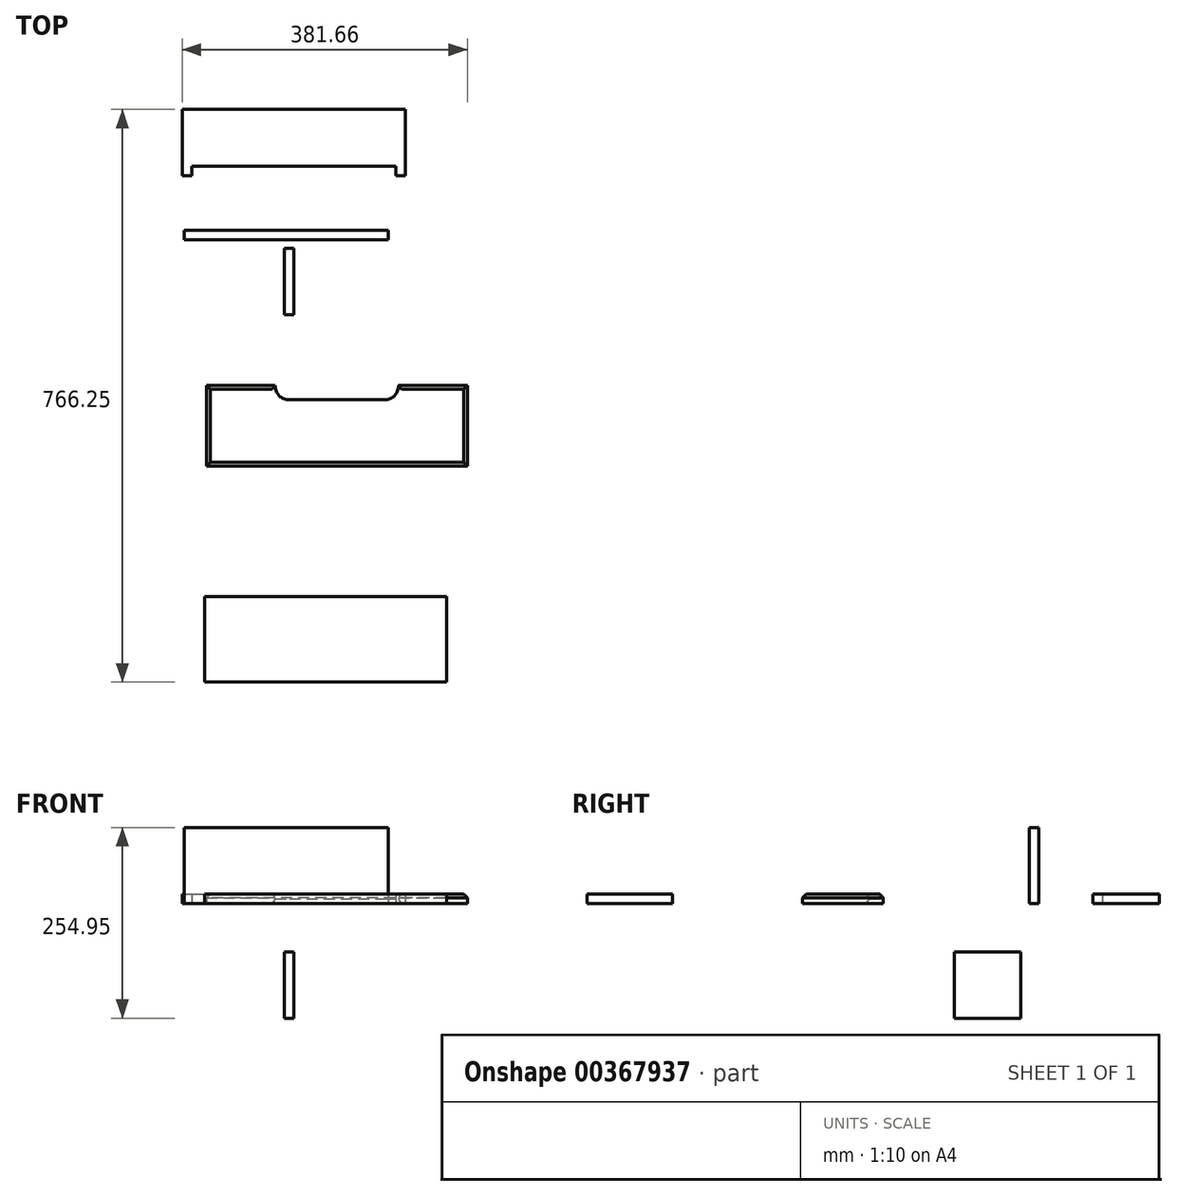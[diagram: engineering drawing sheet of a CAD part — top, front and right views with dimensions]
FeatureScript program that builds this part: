
annotation { "Feature Type Name" : "Feature", "Feature Type Description" : "" }
export const myFeature = defineFeature(function(context is Context, id is Id, definition is map)
    precondition{}
    {
        {
            var Q0;
            Q0=qCreatedBy(makeId("Front.planeOp"),FACE);
            var sketch = newSketch(context, id + "F0", { "sketchPlane" : qUnion([Q0])});
            skLineSegment(sketch, "E0.bottom", {"start": v(-133.55, 101.26) * mm, "end": v(139.5, 101.26) * mm});
            skLineSegment(sketch, "E0.top", {"start": v(-133.55, -0.34) * mm, "end": v(139.5, -0.34) * mm});
            skLineSegment(sketch, "E0.left", {"start": v(-133.55, 101.26) * mm, "end": v(-133.55, -0.34) * mm});
            skLineSegment(sketch, "E0.right", {"start": v(139.5, 101.26) * mm, "end": v(139.5, -0.34) * mm});
            skSolve(sketch);
        }
        {
            var Q0;
            Q0=makeQuery(id+"F0.imprint","IMPRINT",FACE,{"disambiguationData":[TD([[makeQuery(id+"F0.imprint","IMPRINT",EDGE,{"derivedFrom":sQuery(id+"F0.wireOp",EDGE,"E0.bottom")}),-1.0]])]});
            extrude(context, id + "F1", {"entities" : qUnion([Q0]), "depth" : 12.7 * mm});
        }
        {
            var Q0;
            Q0=qCreatedBy(makeId("Top.planeOp"),FACE);
            var sketch = newSketch(context, id + "F2", { "sketchPlane" : qUnion([Q0])});
            skLineSegment(sketch, "E1.bottom", {"start": v(-136.52, 161.62) * mm, "end": v(161.93, 161.62) * mm});
            skLineSegment(sketch, "E1.top", {"start": v(-123.82, 85.42) * mm, "end": v(149.23, 85.42) * mm});
            skLineSegment(sketch, "E1.left", {"start": v(-136.52, 161.62) * mm, "end": v(-136.52, 85.42) * mm});
            skLineSegment(sketch, "E1.right", {"start": v(161.93, 161.62) * mm, "end": v(161.93, 85.42) * mm});
            skLineSegment(sketch, "E2.top", {"start": v(161.93, 72.72) * mm, "end": v(149.23, 72.72) * mm});
            skLineSegment(sketch, "E2.left", {"start": v(161.93, 85.42) * mm, "end": v(161.93, 72.72) * mm});
            skLineSegment(sketch, "E2.right", {"start": v(149.23, 85.42) * mm, "end": v(149.23, 72.72) * mm});
            skLineSegment(sketch, "E3.top", {"start": v(-136.52, 72.72) * mm, "end": v(-123.82, 72.72) * mm});
            skLineSegment(sketch, "E3.left", {"start": v(-136.52, 85.42) * mm, "end": v(-136.52, 72.72) * mm});
            skLineSegment(sketch, "E3.right", {"start": v(-123.82, 85.42) * mm, "end": v(-123.82, 72.72) * mm});
            skSolve(sketch);
        }
        {
            var Q0;
            Q0=makeQuery(id+"F2.imprint","IMPRINT",FACE,{"disambiguationData":[TD([[makeQuery(id+"F2.imprint","IMPRINT",EDGE,{"derivedFrom":sQuery(id+"F2.wireOp",EDGE,"E1.bottom")}),-1.0]])]});
            extrude(context, id + "F3", {"entities" : qUnion([Q0]), "depth" : 12.7 * mm});
        }
        {
            var Q0;
            Q0=qCreatedBy(makeId("Right.planeOp"),FACE);
            var sketch = newSketch(context, id + "F4", { "sketchPlane" : qUnion([Q0])});
            skLineSegment(sketch, "E4.bottom", {"start": v(-24.25, -64.79) * mm, "end": v(-113.15, -64.79) * mm});
            skLineSegment(sketch, "E4.top", {"start": v(-24.25, -153.69) * mm, "end": v(-113.15, -153.69) * mm});
            skLineSegment(sketch, "E4.left", {"start": v(-24.25, -64.79) * mm, "end": v(-24.25, -153.69) * mm});
            skLineSegment(sketch, "E4.right", {"start": v(-113.15, -64.79) * mm, "end": v(-113.15, -153.69) * mm});
            skSolve(sketch);
        }
        {
            var Q0;
            Q0=makeQuery(id+"F4.imprint","IMPRINT",FACE,{"disambiguationData":[TD([[makeQuery(id+"F4.imprint","IMPRINT",EDGE,{"derivedFrom":sQuery(id+"F4.wireOp",EDGE,"E4.bottom")}),1.0]])]});
            extrude(context, id + "F5", {"entities" : qUnion([Q0]), "depth" : 12.7 * mm});
        }
        {
            var Q0;
            Q0=qCreatedBy(makeId("Top.planeOp"),FACE);
            var sketch = newSketch(context, id + "F6", { "sketchPlane" : qUnion([Q0])});
            skLineSegment(sketch, "E5.bottom", {"start": v(-104.11, -207.94) * mm, "end": v(-12.04, -207.94) * mm});
            skLineSegment(sketch, "E5.top", {"start": v(-104.11, -315.89) * mm, "end": v(245.14, -315.89) * mm});
            skLineSegment(sketch, "E5.left", {"start": v(-104.11, -207.94) * mm, "end": v(-104.11, -315.89) * mm});
            skLineSegment(sketch, "E5.right", {"start": v(245.14, -207.94) * mm, "end": v(245.14, -315.89) * mm});
            skArc(sketch, "E6.0.startCap", {"start": v(7.01, -226.99) * mm, "mid": v(-6.46, -221.4) * mm, "end": v(-12.04, -207.94) * mm});
            skArc(sketch, "E6.0.endCap", {"start": v(153.06, -207.94) * mm, "mid": v(147.48, -221.4) * mm, "end": v(134.01, -226.99) * mm});
            skLineSegment(sketch, "E6.0.right", {"start": v(7.01, -226.99) * mm, "end": v(134.01, -226.99) * mm});
            skLineSegment(sketch, "E7.trimOffspring", {"start": v(153.06, -207.94) * mm, "end": v(245.14, -207.94) * mm});
            skSolve(sketch);
        }
        {
            var Q0;
            Q0 = qSketchRegion(id + "F6", true);
            extrude(context, id + "F7", {"entities" : qUnion([Q0]), "depth" : 12.7 * mm});
        }
        {
            var Q0;
            Q0=makeQuery(id+"F7.opExtrude","CAP_EDGE",EDGE,{"disambiguationData":[OSD([sQuery(id+"F6.wireOp",EDGE,"E6.0.right")])],"isStart":false});
            var Q1;
            Q1=makeQuery(id+"F7.opExtrude","CAP_EDGE",EDGE,{"disambiguationData":[OSD([sQuery(id+"F6.wireOp",EDGE,"E6.0.right")])],"isStart":true});
            fillet(context, id + "F8", {"entities" : qUnion([Q0, Q1]), "radius" : 7.62 * mm, "tangentPropagation" : true, "allowEdgeOverflow" : false});
        }
        {
            var Q0;
            Q0=makeQuery(id+"F7.opExtrude","CAP_EDGE",EDGE,{"disambiguationData":[OSD([sQuery(id+"F6.wireOp",EDGE,"E5.bottom")])],"isStart":false});
            var Q1;
            Q1=makeQuery(id+"F7.opExtrude","CAP_EDGE",EDGE,{"disambiguationData":[OSD([sQuery(id+"F6.wireOp",EDGE,"E5.left")])],"isStart":false});
            var Q2;
            Q2=makeQuery(id+"F7.opExtrude","CAP_EDGE",EDGE,{"disambiguationData":[OSD([sQuery(id+"F6.wireOp",EDGE,"E5.top")])],"isStart":false});
            var Q3;
            Q3=makeQuery(id+"F7.opExtrude","CAP_EDGE",EDGE,{"disambiguationData":[OSD([sQuery(id+"F6.wireOp",EDGE,"E5.right")])],"isStart":false});
            var Q4;
            Q4=makeQuery(id+"F7.opExtrude","CAP_EDGE",EDGE,{"disambiguationData":[OSD([sQuery(id+"F6.wireOp",EDGE,"E7.trimOffspring")])],"isStart":false});
            chamfer(context, id + "F9", {"entities" : qUnion([Q0, Q1, Q2, Q3, Q4]), "width" : 5.08 * mm});
        }
        {
            var Q0;
            Q0=qCreatedBy(makeId("Top.planeOp"),FACE);
            var sketch = newSketch(context, id + "F10", { "sketchPlane" : qUnion([Q0])});
            skLineSegment(sketch, "E8.bottom", {"start": v(-106.29, -490.33) * mm, "end": v(217.56, -490.33) * mm});
            skLineSegment(sketch, "E8.top", {"start": v(-106.29, -604.63) * mm, "end": v(217.56, -604.63) * mm});
            skLineSegment(sketch, "E8.left", {"start": v(-106.29, -490.33) * mm, "end": v(-106.29, -604.63) * mm});
            skLineSegment(sketch, "E8.right", {"start": v(217.56, -490.33) * mm, "end": v(217.56, -604.63) * mm});
            skSolve(sketch);
        }
        {
            var Q0;
            Q0=makeQuery(id+"F10.imprint","IMPRINT",FACE,{"disambiguationData":[TD([[makeQuery(id+"F10.imprint","IMPRINT",EDGE,{"derivedFrom":sQuery(id+"F10.wireOp",EDGE,"E8.bottom")}),-1.0]])]});
            extrude(context, id + "F11", {"entities" : qUnion([Q0]), "depth" : 12.7 * mm});
        }
    });
